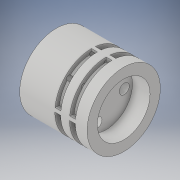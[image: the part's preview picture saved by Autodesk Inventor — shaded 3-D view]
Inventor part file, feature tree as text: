
AUTODESK INVENTOR PART (.ipt)
format: ipt  version: 2019 (Build 230136000, 136)  size: 281,088 bytes
history: native  units: in
note: dims shown in document units (in); Inventor stores cm internally (conversion verified against a paired STEP export)
features: sketch x9, extrude x8, hole x1
ambient origin geometry x8: Origin, YZ Plane, XZ Plane, XY Plane, X Axis, Y Axis, Z Axis, Center Point
bodies: Solid1 (feature_tree)
feature tree (18):
  extrude  "Extrusion1"  Depth=0.8661in
  extrude  "Extrusion2"  Depth=0.2559in
  extrude  "Extrusion3"  Depth=0.0787in TaperAngle=0.0deg
  extrude  "Extrusion4"  Depth=0.0787in TaperAngle=0.0deg
  extrude  "Extrusion5"  Depth=0.2441in
  hole  "Hole1"  [1 undecoded]
  extrude  "Extrusion7"  Depth=0.2756in TaperAngle=0.0deg
  extrude  "Extrusion8"  Depth=0.1575in
  extrude  "Extrusion9"  Depth=0.1575in
  sketch  "Sketch1"  dims[d0=0.9843in d1=0.8661in]
  sketch  "Sketch2"  dims[d2=0.2559in d3=0.0in d4=0.7087in]
  sketch  "Sketch3"  dims[d5=0.2165in d6=0.0in d7=0.0787in d8=0.0in]
  sketch  "Sketch4"  dims[d9=0.1181in d10=0.0in d11=0.0787in d12=0.0in]
  sketch  "Sketch5"  dims[d15=0.2441in d16=0.2441in]
  sketch  "Sketch7"  dims[d17=120.0deg d18=0.2441in]
  sketch  "Sketch8"  dims[d19=120.0deg]
  sketch  "Sketch10"  dims[d20=0.1339in d21=0.75in d22=0.248in d23=0.25in d24=90.0deg d25=1.0in d26=0.8108in d34=0.2756in d35=0.0in]
  sketch  "Sketch11"  dims[d54=0.8661in d55=0.8661in d60=0.0591in d61=0.0591in d62=0.0591in d63=0.0591in d66=0.4331in d67=45.0deg d68=0.0591in d69=0.4331in d70=0.4331in d71=0.4331in d72=0.0591in d73=0.0591in d74=0.0591in d75=0.2756in d76=0.0in d77=0.7087in d78=0.9843in d79=0.1575in d80=0.0in]
note: 1 required parameter value undecoded (feature->parameter linkage not recoverable at this tier; creation-order binding heuristic only, values carry confidence <= 0.55)
